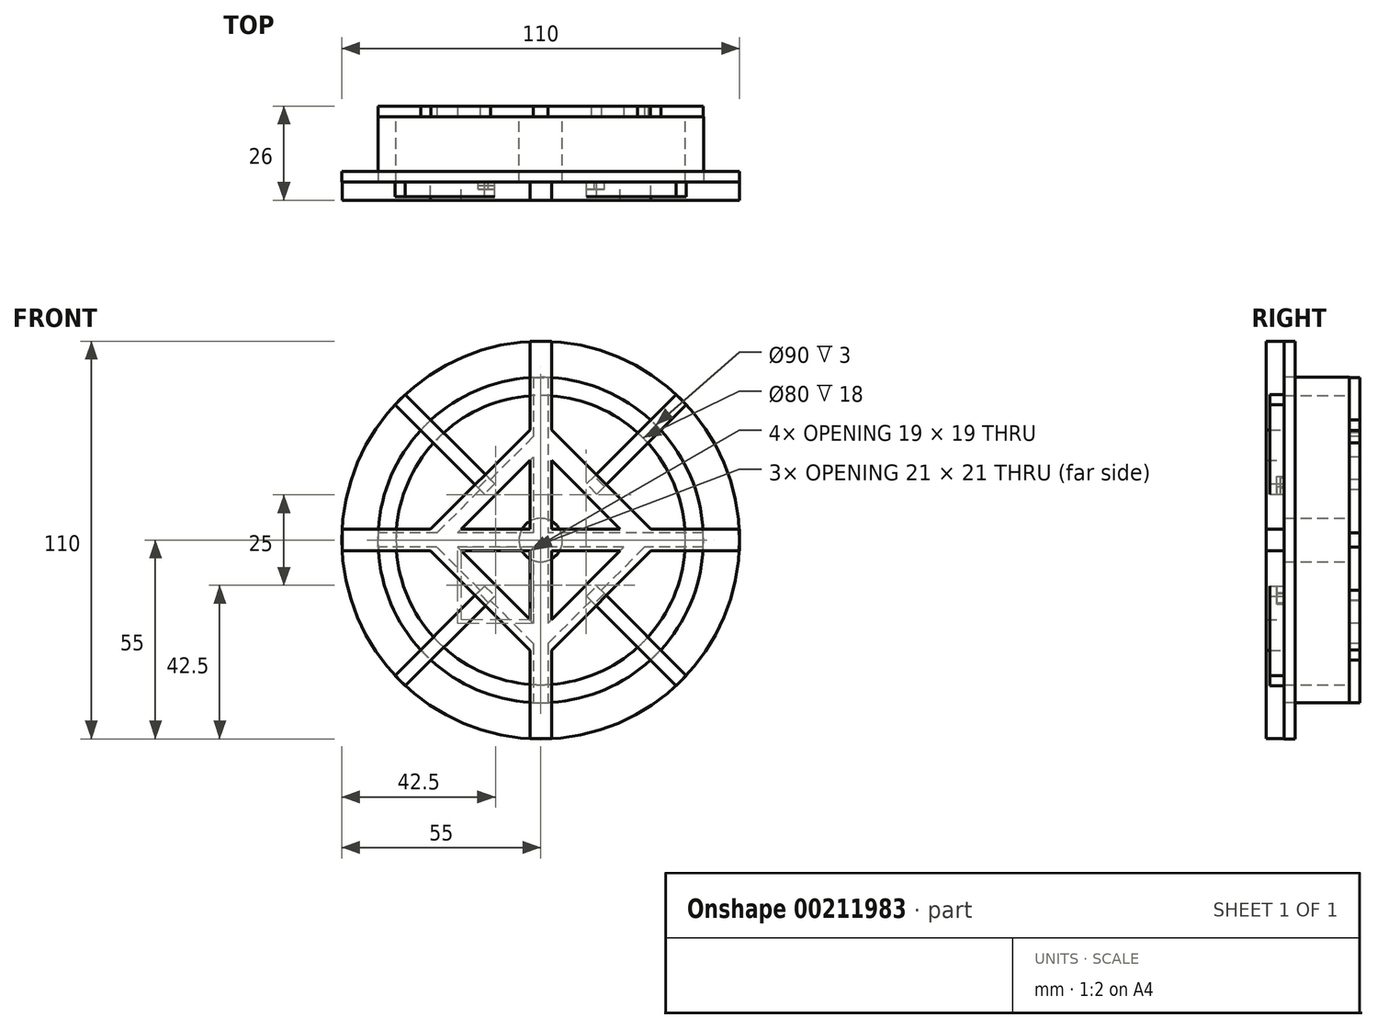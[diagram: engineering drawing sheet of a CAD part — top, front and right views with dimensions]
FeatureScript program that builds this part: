
annotation { "Feature Type Name" : "Feature", "Feature Type Description" : "" }
export const myFeature = defineFeature(function(context is Context, id is Id, definition is map)
    precondition{}
    {
        {
            var Q0;
            Q0=qCreatedBy(makeId("Front.planeOp"),FACE);
            var sketch = newSketch(context, id + "F0", { "sketchPlane" : qUnion([Q0])});
            skCircle(sketch, "E0", {"center": v(0, 0) * mm, "radius": 55 * mm});
            skCircle(sketch, "E1", {"center": v(0, 0) * mm, "radius": 45 * mm});
            skCircle(sketch, "E2", {"center": v(0, 0) * mm, "radius": 6 * mm});
            skCircle(sketch, "E3", {"center": v(0, 0) * mm, "radius": 40 * mm});
            skSolve(sketch);
        }
        {
            var Q0;
            Q0=makeQuery(id+"F0.imprint","IMPRINT",FACE,{"disambiguationData":[TD([[makeQuery(id+"F0.imprint","IMPRINT",EDGE,{"derivedFrom":sQuery(id+"F0.wireOp",EDGE,"E2")}),1.0]])]});
            var Q1;
            Q1=makeQuery(id+"F0.imprint","IMPRINT",FACE,{"disambiguationData":[TD([[makeQuery(id+"F0.imprint","IMPRINT",EDGE,{"derivedFrom":sQuery(id+"F0.wireOp",EDGE,"E1")}),1.0]])]});
            extrude(context, id + "F1", {"entities" : qUnion([Q0, Q1]), "depth" : 18 * mm});
        }
        {
            var Q0;
            Q0=makeQuery(id+"F1.opExtrude","CAP_FACE",FACE,{"disambiguationData":[OSD([sQuery(id+"F0.wireOp",EDGE,"E1"),sQuery(id+"F0.wireOp",EDGE,"E3")])],"isStart":false});
            var sketch = newSketch(context, id + "F2", { "sketchPlane" : qUnion([Q0])});
            skCircle(sketch, "E4", {"center": v(0, 0) * mm, "radius": 55 * mm});
            skCircle(sketch, "E5", {"center": v(0, 0) * mm, "radius": 45 * mm});
            skSolve(sketch);
        }
        {
            var Q0;
            Q0=makeQuery(id+"F2.imprint","IMPRINT",FACE,{"disambiguationData":[TD([[makeQuery(id+"F2.imprint","IMPRINT",EDGE,{"derivedFrom":sQuery(id+"F2.wireOp",EDGE,"E4")}),1.0]])]});
            extrude(context, id + "F3", {"entities" : qUnion([Q0]), "oppositeDirection" : true, "depth" : 3 * mm});
        }
        {
            var Q0;
            Q0=makeQuery(id+"F3.opExtrude","CAP_FACE",FACE,{"disambiguationData":[OSD([sQuery(id+"F2.wireOp",EDGE,"E4"),sQuery(id+"F2.wireOp",EDGE,"E5")])],"isStart":true});
            var sketch = newSketch(context, id + "F4", { "sketchPlane" : qUnion([Q0])});
            skLineSegment(sketch, "E6.bottom", {"start": v(-54.92, -3) * mm, "end": v(54.92, -3) * mm});
            skLineSegment(sketch, "E6.top", {"start": v(-54.92, 3) * mm, "end": v(54.92, 3) * mm});
            skLineSegment(sketch, "E6.left", {"start": v(-54.92, -3) * mm, "end": v(-54.92, 3) * mm});
            skLineSegment(sketch, "E6.right", {"start": v(54.92, -3) * mm, "end": v(54.92, 3) * mm});
            skPoint(sketch, "E6.middle", {"position": v(0, 0) * mm});
            skLineSegment(sketch, "E7.bottom", {"start": v(3, 54.92) * mm, "end": v(-3, 54.92) * mm});
            skLineSegment(sketch, "E7.top", {"start": v(3, -54.92) * mm, "end": v(-3, -54.92) * mm});
            skLineSegment(sketch, "E7.left", {"start": v(3, 54.92) * mm, "end": v(3, -54.92) * mm});
            skLineSegment(sketch, "E7.right", {"start": v(-3, 54.92) * mm, "end": v(-3, -54.92) * mm});
            skLineSegment(sketch, "E8", {"start": v(-142.2, 0) * mm, "end": v(132.52, 0) * mm, "construction": true});
            skLineSegment(sketch, "E9", {"start": v(0, 134.39) * mm, "end": v(0, -130.48) * mm, "construction": true});
            skLineSegment(sketch, "E10", {"start": v(0, 25) * mm, "end": v(-25, 0) * mm});
            skLineSegment(sketch, "E11", {"start": v(-25, 0) * mm, "end": v(0, -25) * mm});
            skLineSegment(sketch, "E12", {"start": v(0, -25) * mm, "end": v(25, 0) * mm});
            skLineSegment(sketch, "E13", {"start": v(25, 0) * mm, "end": v(0, 25) * mm});
            skLineSegment(sketch, "E14", {"start": v(0, 33.49) * mm, "end": v(-33.49, 0) * mm});
            skLineSegment(sketch, "E15", {"start": v(-33.49, 0) * mm, "end": v(0, -33.49) * mm});
            skLineSegment(sketch, "E16", {"start": v(0, -33.49) * mm, "end": v(33.49, 0) * mm});
            skLineSegment(sketch, "E17", {"start": v(33.49, 0) * mm, "end": v(0, 33.49) * mm});
            skSolve(sketch);
        }
        {
            var Q0;
            {var subQ0=sQuery(id+"F4.wireOp",EDGE,"E7.right");var subQ1=sQuery(id+"F4.wireOp",EDGE,"E6.bottom");var subQ2=makeQuery(id+"F4.imprint","INTERSECT",VERTEX,{"derivedFrom":[subQ1,subQ0]});Q0=makeQuery(id+"F4.imprint","IMPRINT",FACE,{"disambiguationData":[TD([[makeQuery(id+"F4.imprint","IMPRINT",EDGE,{"disambiguationData":[TD([[subQ2,-1.0]])],"derivedFrom":subQ1}),1.0]])]});}
            var Q1;
            {var subQ0=sQuery(id+"F4.wireOp",EDGE,"E6.left");Q1=makeQuery(id+"F4.imprint","IMPRINT",FACE,{"disambiguationData":[TD([[makeQuery(id+"F4.imprint","IMPRINT",EDGE,{"derivedFrom":subQ0}),-1.0]])]});}
            var Q2;
            {var subQ0=sQuery(id+"F4.wireOp",EDGE,"E7.right");var subQ1=sQuery(id+"F4.wireOp",EDGE,"E6.bottom");var subQ2=makeQuery(id+"F4.imprint","INTERSECT",VERTEX,{"derivedFrom":[subQ1,subQ0]});Q2=makeQuery(id+"F4.imprint","IMPRINT",FACE,{"disambiguationData":[TD([[makeQuery(id+"F4.imprint","IMPRINT",EDGE,{"disambiguationData":[TD([[subQ2,1.0]])],"derivedFrom":subQ1}),1.0]])]});}
            var Q3;
            {var subQ0=sQuery(id+"F4.wireOp",EDGE,"E7.right");var subQ1=sQuery(id+"F4.wireOp",EDGE,"E6.bottom");var subQ2=makeQuery(id+"F4.imprint","INTERSECT",VERTEX,{"derivedFrom":[subQ1,subQ0]});Q3=makeQuery(id+"F4.imprint","IMPRINT",FACE,{"disambiguationData":[TD([[makeQuery(id+"F4.imprint","IMPRINT",EDGE,{"disambiguationData":[TD([[subQ2,-1.0]])],"derivedFrom":subQ1}),-1.0]])]});}
            var Q4;
            {var subQ0=sQuery(id+"F4.wireOp",EDGE,"E7.left");var subQ1=sQuery(id+"F4.wireOp",EDGE,"E6.bottom");var subQ2=makeQuery(id+"F4.imprint","INTERSECT",VERTEX,{"derivedFrom":[subQ1,subQ0]});Q4=makeQuery(id+"F4.imprint","IMPRINT",FACE,{"disambiguationData":[TD([[makeQuery(id+"F4.imprint","IMPRINT",EDGE,{"disambiguationData":[TD([[subQ2,-1.0]])],"derivedFrom":subQ1}),1.0]])]});}
            var Q5;
            {var subQ0=sQuery(id+"F4.wireOp",EDGE,"E6.right");Q5=makeQuery(id+"F4.imprint","IMPRINT",FACE,{"disambiguationData":[TD([[makeQuery(id+"F4.imprint","IMPRINT",EDGE,{"derivedFrom":subQ0}),1.0]])]});}
            var Q6;
            {var subQ0=sQuery(id+"F4.wireOp",EDGE,"E7.bottom");Q6=makeQuery(id+"F4.imprint","IMPRINT",FACE,{"disambiguationData":[TD([[makeQuery(id+"F4.imprint","IMPRINT",EDGE,{"derivedFrom":subQ0}),1.0]])]});}
            var Q7;
            {var subQ0=sQuery(id+"F4.wireOp",EDGE,"E7.top");Q7=makeQuery(id+"F4.imprint","IMPRINT",FACE,{"disambiguationData":[TD([[makeQuery(id+"F4.imprint","IMPRINT",EDGE,{"derivedFrom":subQ0}),-1.0]])]});}
            var Q8;
            {var subQ0=sQuery(id+"F4.wireOp",EDGE,"E7.right");var subQ1=sQuery(id+"F4.wireOp",EDGE,"E6.top");var subQ2=makeQuery(id+"F4.imprint","INTERSECT",VERTEX,{"derivedFrom":[subQ1,subQ0]});Q8=makeQuery(id+"F4.imprint","IMPRINT",FACE,{"disambiguationData":[TD([[makeQuery(id+"F4.imprint","IMPRINT",EDGE,{"disambiguationData":[TD([[subQ2,-1.0]])],"derivedFrom":subQ1}),1.0]])]});}
            var Q9;
            {var subQ0=sQuery(id+"F4.wireOp",EDGE,"E15");var subQ5=sQuery(id+"F4.wireOp",EDGE,"E6.bottom");var subQ6=makeQuery(id+"F4.imprint","INTERSECT",VERTEX,{"derivedFrom":[subQ5,subQ0]});Q9=makeQuery(id+"F4.imprint","IMPRINT",FACE,{"disambiguationData":[TD([[makeQuery(id+"F4.imprint","IMPRINT",EDGE,{"disambiguationData":[TD([[subQ6,1.0]])],"derivedFrom":subQ5}),1.0]])]});}
            var Q10;
            {var subQ3=sQuery(id+"F4.wireOp",EDGE,"E6.bottom");var subQ9=sQuery(id+"F4.wireOp",EDGE,"E15");var subQ10=makeQuery(id+"F4.imprint","INTERSECT",VERTEX,{"derivedFrom":[subQ3,subQ9]});Q10=makeQuery(id+"F4.imprint","IMPRINT",FACE,{"disambiguationData":[TD([[makeQuery(id+"F4.imprint","IMPRINT",EDGE,{"disambiguationData":[TD([[subQ10,-1.0]])],"derivedFrom":subQ3}),1.0]])]});}
            var Q11;
            {var subQ0=sQuery(id+"F4.wireOp",EDGE,"E14");var subQ1=sQuery(id+"F4.wireOp",EDGE,"E6.top");var subQ2=makeQuery(id+"F4.imprint","INTERSECT",VERTEX,{"derivedFrom":[subQ1,subQ0]});Q11=makeQuery(id+"F4.imprint","IMPRINT",FACE,{"disambiguationData":[TD([[makeQuery(id+"F4.imprint","IMPRINT",EDGE,{"disambiguationData":[TD([[subQ2,-1.0]])],"derivedFrom":subQ1}),1.0]])]});}
            var Q12;
            {var subQ0=sQuery(id+"F4.wireOp",EDGE,"E15");var subQ1=sQuery(id+"F4.wireOp",EDGE,"E6.bottom");var subQ2=makeQuery(id+"F4.imprint","INTERSECT",VERTEX,{"derivedFrom":[subQ1,subQ0]});Q12=makeQuery(id+"F4.imprint","IMPRINT",FACE,{"disambiguationData":[TD([[makeQuery(id+"F4.imprint","IMPRINT",EDGE,{"disambiguationData":[TD([[subQ2,-1.0]])],"derivedFrom":subQ1}),-1.0]])]});}
            var Q13;
            {var subQ0=sQuery(id+"F4.wireOp",EDGE,"E12");var subQ1=sQuery(id+"F4.wireOp",EDGE,"E6.bottom");var subQ2=makeQuery(id+"F4.imprint","INTERSECT",VERTEX,{"derivedFrom":[subQ1,subQ0]});Q13=makeQuery(id+"F4.imprint","IMPRINT",FACE,{"disambiguationData":[TD([[makeQuery(id+"F4.imprint","IMPRINT",EDGE,{"disambiguationData":[TD([[subQ2,-1.0]])],"derivedFrom":subQ1}),-1.0]])]});}
            var Q14;
            {var subQ0=sQuery(id+"F4.wireOp",EDGE,"E12");var subQ9=sQuery(id+"F4.wireOp",EDGE,"E7.left");var subQ11=makeQuery(id+"F4.imprint","INTERSECT",VERTEX,{"derivedFrom":[subQ9,subQ0]});Q14=makeQuery(id+"F4.imprint","IMPRINT",FACE,{"disambiguationData":[TD([[makeQuery(id+"F4.imprint","IMPRINT",EDGE,{"disambiguationData":[TD([[subQ11,-1.0]])],"derivedFrom":subQ9}),-1.0]])]});}
            var Q15;
            {var subQ0=sQuery(id+"F4.wireOp",EDGE,"E16");var subQ5=sQuery(id+"F4.wireOp",EDGE,"E7.left");var subQ6=makeQuery(id+"F4.imprint","INTERSECT",VERTEX,{"derivedFrom":[subQ5,subQ0]});Q15=makeQuery(id+"F4.imprint","IMPRINT",FACE,{"disambiguationData":[TD([[makeQuery(id+"F4.imprint","IMPRINT",EDGE,{"disambiguationData":[TD([[subQ6,-1.0]])],"derivedFrom":subQ5}),-1.0]])]});}
            var Q16;
            {var subQ0=sQuery(id+"F4.wireOp",EDGE,"E13");var subQ1=sQuery(id+"F4.wireOp",EDGE,"E6.top");var subQ2=makeQuery(id+"F4.imprint","INTERSECT",VERTEX,{"derivedFrom":[subQ1,subQ0]});Q16=makeQuery(id+"F4.imprint","IMPRINT",FACE,{"disambiguationData":[TD([[makeQuery(id+"F4.imprint","IMPRINT",EDGE,{"disambiguationData":[TD([[subQ2,-1.0]])],"derivedFrom":subQ1}),1.0]])]});}
            var Q17;
            {var subQ1=sQuery(id+"F4.wireOp",EDGE,"E12");var subQ5=sQuery(id+"F4.wireOp",EDGE,"E6.bottom");var subQ6=makeQuery(id+"F4.imprint","INTERSECT",VERTEX,{"derivedFrom":[subQ5,subQ1]});Q17=makeQuery(id+"F4.imprint","IMPRINT",FACE,{"disambiguationData":[TD([[makeQuery(id+"F4.imprint","IMPRINT",EDGE,{"disambiguationData":[TD([[subQ6,-1.0]])],"derivedFrom":subQ5}),1.0]])]});}
            var Q18;
            {var subQ3=sQuery(id+"F4.wireOp",EDGE,"E7.left");var subQ9=sQuery(id+"F4.wireOp",EDGE,"E17");var subQ10=makeQuery(id+"F4.imprint","INTERSECT",VERTEX,{"derivedFrom":[subQ3,subQ9]});Q18=makeQuery(id+"F4.imprint","IMPRINT",FACE,{"disambiguationData":[TD([[makeQuery(id+"F4.imprint","IMPRINT",EDGE,{"disambiguationData":[TD([[subQ10,-1.0]])],"derivedFrom":subQ3}),-1.0]])]});}
            var Q19;
            {var subQ0=sQuery(id+"F4.wireOp",EDGE,"E17");var subQ5=sQuery(id+"F4.wireOp",EDGE,"E7.left");var subQ6=makeQuery(id+"F4.imprint","INTERSECT",VERTEX,{"derivedFrom":[subQ5,subQ0]});Q19=makeQuery(id+"F4.imprint","IMPRINT",FACE,{"disambiguationData":[TD([[makeQuery(id+"F4.imprint","IMPRINT",EDGE,{"disambiguationData":[TD([[subQ6,1.0]])],"derivedFrom":subQ5}),-1.0]])]});}
            var Q20;
            {var subQ1=sQuery(id+"F4.wireOp",EDGE,"E16");var subQ5=sQuery(id+"F4.wireOp",EDGE,"E6.bottom");var subQ6=makeQuery(id+"F4.imprint","INTERSECT",VERTEX,{"derivedFrom":[subQ5,subQ1]});Q20=makeQuery(id+"F4.imprint","IMPRINT",FACE,{"disambiguationData":[TD([[makeQuery(id+"F4.imprint","IMPRINT",EDGE,{"disambiguationData":[TD([[subQ6,-1.0]])],"derivedFrom":subQ5}),1.0]])]});}
            extrude(context, id + "F5", {"entities" : qUnion([Q0, Q1, Q2, Q3, Q4, Q5, Q6, Q7, Q8, Q9, Q10, Q11, Q12, Q13, Q14, Q15, Q16, Q17, Q18, Q19, Q20]), "depth" : 5 * mm});
        }
        {
            var Q0;
            Q0=makeQuery(id+"F3.opExtrude","CAP_FACE",FACE,{"disambiguationData":[OSD([sQuery(id+"F2.wireOp",EDGE,"E4"),sQuery(id+"F2.wireOp",EDGE,"E5")])],"isStart":true});
            var sketch = newSketch(context, id + "F6", { "sketchPlane" : qUnion([Q0])});
            skLineSegment(sketch, "E18", {"start": v(116.81, -116.81) * mm, "end": v(-97.26, 97.26) * mm, "construction": true});
            skLineSegment(sketch, "E19", {"start": v(-138.56, 0) * mm, "end": v(133.7, 0) * mm, "construction": true});
            skLineSegment(sketch, "E20", {"start": v(0, 132.87) * mm, "end": v(0, -131.26) * mm, "construction": true});
            skLineSegment(sketch, "E21", {"start": v(-110.25, -110.25) * mm, "end": v(110.73, 110.73) * mm, "construction": true});
            skLineSegment(sketch, "E22", {"start": v(-15.53, 12.7) * mm, "end": v(-40.28, 37.45) * mm});
            skLineSegment(sketch, "E23", {"start": v(-40.28, 37.45) * mm, "end": v(-37.45, 40.28) * mm});
            skLineSegment(sketch, "E24", {"start": v(-37.45, 40.28) * mm, "end": v(-12.7, 15.53) * mm});
            skLineSegment(sketch, "E25", {"start": v(-12.7, 15.53) * mm, "end": v(-15.53, 12.7) * mm});
            skPoint(sketch, "E26.center", {"position": v(0, -14.16) * mm});
            skPoint(sketch, "E27.center", {"position": v(0, -31.9) * mm});
            skLineSegment(sketch, "E28.1.0", {"start": v(-40.28, -37.45) * mm, "end": v(-15.53, -12.7) * mm});
            skLineSegment(sketch, "E28.1.1", {"start": v(-37.45, -40.28) * mm, "end": v(-40.28, -37.45) * mm});
            skLineSegment(sketch, "E28.1.2", {"start": v(-12.7, -15.53) * mm, "end": v(-37.45, -40.28) * mm});
            skLineSegment(sketch, "E28.1.3", {"start": v(-15.53, -12.7) * mm, "end": v(-12.7, -15.53) * mm});
            skLineSegment(sketch, "E28.2.0", {"start": v(37.45, -40.28) * mm, "end": v(12.7, -15.53) * mm});
            skLineSegment(sketch, "E28.2.1", {"start": v(40.28, -37.45) * mm, "end": v(37.45, -40.28) * mm});
            skLineSegment(sketch, "E28.2.2", {"start": v(15.53, -12.7) * mm, "end": v(40.28, -37.45) * mm});
            skLineSegment(sketch, "E28.2.3", {"start": v(12.7, -15.53) * mm, "end": v(15.53, -12.7) * mm});
            skLineSegment(sketch, "E28.3.0", {"start": v(40.28, 37.45) * mm, "end": v(15.53, 12.7) * mm});
            skLineSegment(sketch, "E28.3.1", {"start": v(37.45, 40.28) * mm, "end": v(40.28, 37.45) * mm});
            skLineSegment(sketch, "E28.3.2", {"start": v(12.7, 15.53) * mm, "end": v(37.45, 40.28) * mm});
            skLineSegment(sketch, "E28.3.3", {"start": v(15.53, 12.7) * mm, "end": v(12.7, 15.53) * mm});
            skPoint(sketch, "E28.center", {"position": v(0, 0) * mm});
            skSolve(sketch);
        }
        {
            var Q0;
            Q0 = qSketchRegion(id + "F6", true);
            extrude(context, id + "F7", {"entities" : qUnion([Q0]), "depth" : 4 * mm});
        }
        {
            var Q0;
            Q0=makeQuery(id+"F7.opExtrude","CAP_FACE",FACE,{"disambiguationData":[OSD([sQuery(id+"F6.wireOp",EDGE,"E22"),sQuery(id+"F6.wireOp",EDGE,"E23"),sQuery(id+"F6.wireOp",EDGE,"E24"),sQuery(id+"F6.wireOp",EDGE,"E25")])],"isStart":true});
            var sketch = newSketch(context, id + "F8", { "sketchPlane" : qUnion([Q0])});
            skLineSegment(sketch, "E29", {"start": v(14.47, 17.3) * mm, "end": v(12.7, 15.53) * mm});
            skLineSegment(sketch, "E30", {"start": v(12.7, 15.53) * mm, "end": v(15.53, 12.7) * mm});
            skLineSegment(sketch, "E31", {"start": v(15.53, 12.7) * mm, "end": v(17.3, 14.47) * mm});
            skLineSegment(sketch, "E32", {"start": v(17.3, 14.47) * mm, "end": v(14.47, 17.3) * mm});
            skSolve(sketch);
        }
        {
            var Q0;
            Q0=makeQuery(id+"F8.imprint","IMPRINT",FACE,{"disambiguationData":[TD([[makeQuery(id+"F8.imprint","IMPRINT",EDGE,{"derivedFrom":sQuery(id+"F8.wireOp",EDGE,"E29")}),1.0]])]});
            extrude(context, id + "F9", {"entities" : qUnion([Q0]), "operationType" : NewBodyOperationType.REMOVE, "oppositeDirection" : true, "depth" : 1 * mm});
        }
        {
            var Q0;
            Q0=makeQuery(id+"F7.opExtrude","CAP_FACE",FACE,{"disambiguationData":[OSD([sQuery(id+"F6.wireOp",EDGE,"E28.1.0"),sQuery(id+"F6.wireOp",EDGE,"E28.1.1"),sQuery(id+"F6.wireOp",EDGE,"E28.1.2"),sQuery(id+"F6.wireOp",EDGE,"E28.1.3")])],"isStart":true});
            var sketch = newSketch(context, id + "F10", { "sketchPlane" : qUnion([Q0])});
            skLineSegment(sketch, "E33", {"start": v(15.53, -12.7) * mm, "end": v(12.7, -15.53) * mm});
            skLineSegment(sketch, "E34", {"start": v(12.7, -15.53) * mm, "end": v(14.47, -17.3) * mm});
            skLineSegment(sketch, "E35", {"start": v(14.47, -17.3) * mm, "end": v(17.3, -14.47) * mm});
            skLineSegment(sketch, "E36", {"start": v(17.3, -14.47) * mm, "end": v(15.53, -12.7) * mm});
            skSolve(sketch);
        }
        {
            var Q0;
            Q0 = qSketchRegion(id + "F10", true);
            extrude(context, id + "F11", {"entities" : qUnion([Q0]), "operationType" : NewBodyOperationType.REMOVE, "oppositeDirection" : true, "depth" : 2 * mm});
        }
        {
            var Q0;
            Q0=makeQuery(id+"F7.opExtrude","CAP_FACE",FACE,{"disambiguationData":[OSD([sQuery(id+"F6.wireOp",EDGE,"E28.2.0"),sQuery(id+"F6.wireOp",EDGE,"E28.2.1"),sQuery(id+"F6.wireOp",EDGE,"E28.2.2"),sQuery(id+"F6.wireOp",EDGE,"E28.2.3")])],"isStart":true});
            var sketch = newSketch(context, id + "F12", { "sketchPlane" : qUnion([Q0])});
            skLineSegment(sketch, "E37", {"start": v(-12.7, -15.53) * mm, "end": v(-15.53, -12.7) * mm});
            skLineSegment(sketch, "E38", {"start": v(-15.53, -12.7) * mm, "end": v(-17.65, -14.82) * mm});
            skLineSegment(sketch, "E39", {"start": v(-17.65, -14.82) * mm, "end": v(-14.82, -17.65) * mm});
            skLineSegment(sketch, "E40", {"start": v(-14.82, -17.65) * mm, "end": v(-12.7, -15.53) * mm});
            skSolve(sketch);
        }
        {
            var Q0;
            Q0=makeQuery(id+"F12.imprint","IMPRINT",FACE,{"disambiguationData":[TD([[makeQuery(id+"F12.imprint","IMPRINT",EDGE,{"derivedFrom":sQuery(id+"F12.wireOp",EDGE,"E37")}),1.0]])]});
            extrude(context, id + "F13", {"entities" : qUnion([Q0]), "operationType" : NewBodyOperationType.REMOVE, "oppositeDirection" : true, "depth" : 2 * mm});
        }
        {
            var Q0;
            Q0=makeQuery(id+"F7.opExtrude","CAP_FACE",FACE,{"disambiguationData":[OSD([sQuery(id+"F6.wireOp",EDGE,"E28.3.0"),sQuery(id+"F6.wireOp",EDGE,"E28.3.1"),sQuery(id+"F6.wireOp",EDGE,"E28.3.2"),sQuery(id+"F6.wireOp",EDGE,"E28.3.3")])],"isStart":true});
            var sketch = newSketch(context, id + "F14", { "sketchPlane" : qUnion([Q0])});
            skLineSegment(sketch, "E41", {"start": v(-12.7, 15.53) * mm, "end": v(-15.53, 12.7) * mm});
            skLineSegment(sketch, "E42", {"start": v(-15.53, 12.7) * mm, "end": v(-17.65, 14.82) * mm});
            skLineSegment(sketch, "E43", {"start": v(-17.65, 14.82) * mm, "end": v(-14.82, 17.65) * mm});
            skLineSegment(sketch, "E44", {"start": v(-14.82, 17.65) * mm, "end": v(-12.7, 15.53) * mm});
            skSolve(sketch);
        }
        {
            var Q0;
            Q0 = qSketchRegion(id + "F14", true);
            extrude(context, id + "F15", {"entities" : qUnion([Q0]), "operationType" : NewBodyOperationType.REMOVE, "oppositeDirection" : true, "depth" : 2 * mm});
        }
        {
            var Q0;
            Q0=makeQuery(id+"F1.opExtrude","CAP_FACE",FACE,{"disambiguationData":[OSD([sQuery(id+"F0.wireOp",EDGE,"E1"),sQuery(id+"F0.wireOp",EDGE,"E3")])],"isStart":true});
            var sketch = newSketch(context, id + "F16", { "sketchPlane" : qUnion([Q0])});
            skLineSegment(sketch, "E45", {"start": v(-62.44, 0) * mm, "end": v(62.34, 0) * mm, "construction": true});
            skLineSegment(sketch, "E46", {"start": v(0, -61) * mm, "end": v(0, 59.36) * mm, "construction": true});
            skLineSegment(sketch, "E47", {"start": v(-48.21, 48.21) * mm, "end": v(50.02, -50.02) * mm, "construction": true});
            skLineSegment(sketch, "E48", {"start": v(46.02, 46.02) * mm, "end": v(-48.3, -48.3) * mm, "construction": true});
            skLineSegment(sketch, "E49.bottom", {"start": v(-44.96, -2) * mm, "end": v(44.96, -2) * mm});
            skLineSegment(sketch, "E49.top", {"start": v(-44.96, 2) * mm, "end": v(44.96, 2) * mm});
            skLineSegment(sketch, "E49.left", {"start": v(-44.96, -2) * mm, "end": v(-44.96, 2) * mm});
            skLineSegment(sketch, "E49.right", {"start": v(44.96, -2) * mm, "end": v(44.96, 2) * mm});
            skPoint(sketch, "E49.middle", {"position": v(0, 0) * mm});
            skLineSegment(sketch, "E50.bottom", {"start": v(2, 44.96) * mm, "end": v(-2, 44.96) * mm});
            skLineSegment(sketch, "E50.top", {"start": v(2, -44.96) * mm, "end": v(-2, -44.96) * mm});
            skLineSegment(sketch, "E50.left", {"start": v(2, 44.96) * mm, "end": v(2, -44.96) * mm});
            skLineSegment(sketch, "E50.right", {"start": v(-2, 44.96) * mm, "end": v(-2, -44.96) * mm});
            skLineSegment(sketch, "E51", {"start": v(0, 30.66) * mm, "end": v(-30.66, 0) * mm});
            skLineSegment(sketch, "E52", {"start": v(-30.66, 0) * mm, "end": v(0, -30.66) * mm});
            skLineSegment(sketch, "E53", {"start": v(0, -30.66) * mm, "end": v(30.66, 0) * mm});
            skLineSegment(sketch, "E54", {"start": v(30.66, 0) * mm, "end": v(0, 30.66) * mm});
            skLineSegment(sketch, "E55", {"start": v(0, 25) * mm, "end": v(-25, 0) * mm});
            skLineSegment(sketch, "E56", {"start": v(-25, 0) * mm, "end": v(0, -25) * mm});
            skLineSegment(sketch, "E57", {"start": v(0, -25) * mm, "end": v(25, 0) * mm});
            skLineSegment(sketch, "E58", {"start": v(25, 0) * mm, "end": v(0, 25) * mm});
            skLineSegment(sketch, "E59", {"start": v(-16.74, 13.91) * mm, "end": v(-33.2, 30.37) * mm});
            skLineSegment(sketch, "E60", {"start": v(-33.2, 30.37) * mm, "end": v(-30.37, 33.2) * mm});
            skLineSegment(sketch, "E61", {"start": v(-30.37, 33.2) * mm, "end": v(-13.91, 16.74) * mm});
            skLineSegment(sketch, "E62", {"start": v(-13.91, 16.74) * mm, "end": v(-16.74, 13.91) * mm});
            skLineSegment(sketch, "E63.1.0", {"start": v(-33.19, -30.36) * mm, "end": v(-16.73, -13.9) * mm});
            skLineSegment(sketch, "E63.1.1", {"start": v(-13.9, -16.73) * mm, "end": v(-30.36, -33.19) * mm});
            skLineSegment(sketch, "E63.1.2", {"start": v(-30.36, -33.19) * mm, "end": v(-33.19, -30.36) * mm});
            skLineSegment(sketch, "E63.2.0", {"start": v(30.37, -33.17) * mm, "end": v(13.91, -16.71) * mm});
            skLineSegment(sketch, "E63.2.1", {"start": v(16.74, -13.88) * mm, "end": v(33.2, -30.34) * mm});
            skLineSegment(sketch, "E63.2.2", {"start": v(33.2, -30.34) * mm, "end": v(30.37, -33.17) * mm});
            skLineSegment(sketch, "E63.3.0", {"start": v(33.19, 30.4) * mm, "end": v(16.73, 13.93) * mm});
            skLineSegment(sketch, "E63.3.1", {"start": v(13.9, 16.76) * mm, "end": v(30.36, 33.22) * mm});
            skLineSegment(sketch, "E63.3.2", {"start": v(30.36, 33.22) * mm, "end": v(33.19, 30.4) * mm});
            skPoint(sketch, "E63.center", {"position": v(0, 0.02) * mm});
            skSolve(sketch);
        }
        {
            var Q0;
            {var subQ0=sQuery(id+"F16.wireOp",EDGE,"E62");Q0=makeQuery(id+"F16.imprint","IMPRINT",FACE,{"disambiguationData":[TD([[makeQuery(id+"F16.imprint","IMPRINT",EDGE,{"derivedFrom":subQ0}),-1.0]])]});}
            var Q1;
            {var subQ0=sQuery(id+"F16.wireOp",EDGE,"E60");Q1=makeQuery(id+"F16.imprint","IMPRINT",FACE,{"disambiguationData":[TD([[makeQuery(id+"F16.imprint","IMPRINT",EDGE,{"derivedFrom":subQ0}),-1.0]])]});}
            var Q2;
            {var subQ0=sQuery(id+"F16.wireOp",EDGE,"E50.bottom");Q2=makeQuery(id+"F16.imprint","IMPRINT",FACE,{"disambiguationData":[TD([[makeQuery(id+"F16.imprint","IMPRINT",EDGE,{"derivedFrom":subQ0}),1.0]])]});}
            var Q3;
            {var subQ0=sQuery(id+"F16.wireOp",EDGE,"E54");var subQ3=sQuery(id+"F16.wireOp",EDGE,"E50.left");var subQ4=makeQuery(id+"F16.imprint","INTERSECT",VERTEX,{"derivedFrom":[subQ3,subQ0]});Q3=makeQuery(id+"F16.imprint","IMPRINT",FACE,{"disambiguationData":[TD([[makeQuery(id+"F16.imprint","IMPRINT",EDGE,{"disambiguationData":[TD([[subQ4,1.0]])],"derivedFrom":subQ3}),-1.0]])]});}
            var Q4;
            {var subQ0=sQuery(id+"F16.wireOp",EDGE,"E63.3.2");Q4=makeQuery(id+"F16.imprint","IMPRINT",FACE,{"disambiguationData":[TD([[makeQuery(id+"F16.imprint","IMPRINT",EDGE,{"derivedFrom":subQ0}),-1.0]])]});}
            var Q5;
            {var subQ0=sQuery(id+"F16.wireOp",EDGE,"E63.3.0");var subQ1=sQuery(id+"F16.wireOp",EDGE,"E54");var subQ2=makeQuery(id+"F16.imprint","INTERSECT",VERTEX,{"derivedFrom":[subQ1,subQ0]});Q5=makeQuery(id+"F16.imprint","IMPRINT",FACE,{"disambiguationData":[TD([[makeQuery(id+"F16.imprint","IMPRINT",EDGE,{"disambiguationData":[TD([[subQ2,-1.0]])],"derivedFrom":subQ1}),-1.0]])]});}
            var Q6;
            {var subQ2=sQuery(id+"F16.wireOp",EDGE,"E49.top");var subQ6=sQuery(id+"F16.wireOp",EDGE,"E58");var subQ9=makeQuery(id+"F16.imprint","INTERSECT",VERTEX,{"derivedFrom":[subQ2,subQ6]});Q6=makeQuery(id+"F16.imprint","IMPRINT",FACE,{"disambiguationData":[TD([[makeQuery(id+"F16.imprint","IMPRINT",EDGE,{"disambiguationData":[TD([[subQ9,-1.0]])],"derivedFrom":subQ2}),1.0]])]});}
            var Q7;
            {var subQ0=sQuery(id+"F16.wireOp",EDGE,"E54");var subQ3=sQuery(id+"F16.wireOp",EDGE,"E50.left");var subQ4=makeQuery(id+"F16.imprint","INTERSECT",VERTEX,{"derivedFrom":[subQ3,subQ0]});Q7=makeQuery(id+"F16.imprint","IMPRINT",FACE,{"disambiguationData":[TD([[makeQuery(id+"F16.imprint","IMPRINT",EDGE,{"disambiguationData":[TD([[subQ4,-1.0]])],"derivedFrom":subQ3}),-1.0]])]});}
            var Q8;
            {var subQ0=sQuery(id+"F16.wireOp",EDGE,"E62");Q8=makeQuery(id+"F16.imprint","IMPRINT",FACE,{"disambiguationData":[TD([[makeQuery(id+"F16.imprint","IMPRINT",EDGE,{"derivedFrom":subQ0}),1.0]])]});}
            var Q9;
            {var subQ0=sQuery(id+"F16.wireOp",EDGE,"E52");var subQ3=sQuery(id+"F16.wireOp",EDGE,"E49.bottom");var subQ4=makeQuery(id+"F16.imprint","INTERSECT",VERTEX,{"derivedFrom":[subQ3,subQ0]});Q9=makeQuery(id+"F16.imprint","IMPRINT",FACE,{"disambiguationData":[TD([[makeQuery(id+"F16.imprint","IMPRINT",EDGE,{"disambiguationData":[TD([[subQ4,-1.0]])],"derivedFrom":subQ3}),1.0]])]});}
            var Q10;
            {var subQ0=sQuery(id+"F16.wireOp",EDGE,"E52");var subQ3=sQuery(id+"F16.wireOp",EDGE,"E49.bottom");var subQ4=makeQuery(id+"F16.imprint","INTERSECT",VERTEX,{"derivedFrom":[subQ3,subQ0]});Q10=makeQuery(id+"F16.imprint","IMPRINT",FACE,{"disambiguationData":[TD([[makeQuery(id+"F16.imprint","IMPRINT",EDGE,{"disambiguationData":[TD([[subQ4,1.0]])],"derivedFrom":subQ3}),1.0]])]});}
            var Q11;
            {var subQ0=sQuery(id+"F16.wireOp",EDGE,"E52");var subQ3=sQuery(id+"F16.wireOp",EDGE,"E49.bottom");var subQ4=makeQuery(id+"F16.imprint","INTERSECT",VERTEX,{"derivedFrom":[subQ3,subQ0]});Q11=makeQuery(id+"F16.imprint","IMPRINT",FACE,{"disambiguationData":[TD([[makeQuery(id+"F16.imprint","IMPRINT",EDGE,{"disambiguationData":[TD([[subQ4,-1.0]])],"derivedFrom":subQ3}),-1.0]])]});}
            var Q12;
            {var subQ5=sQuery(id+"F16.wireOp",EDGE,"E56");var subQ7=sQuery(id+"F16.wireOp",EDGE,"E49.bottom");var subQ9=makeQuery(id+"F16.imprint","INTERSECT",VERTEX,{"derivedFrom":[subQ7,subQ5]});Q12=makeQuery(id+"F16.imprint","IMPRINT",FACE,{"disambiguationData":[TD([[makeQuery(id+"F16.imprint","IMPRINT",EDGE,{"disambiguationData":[TD([[subQ9,-1.0]])],"derivedFrom":subQ7}),1.0]])]});}
            var Q13;
            {var subQ3=sQuery(id+"F16.wireOp",EDGE,"E49.bottom");var subQ5=sQuery(id+"F16.wireOp",EDGE,"E50.left");var subQ6=makeQuery(id+"F16.imprint","INTERSECT",VERTEX,{"derivedFrom":[subQ3,subQ5]});Q13=makeQuery(id+"F16.imprint","IMPRINT",FACE,{"disambiguationData":[TD([[makeQuery(id+"F16.imprint","IMPRINT",EDGE,{"disambiguationData":[TD([[subQ6,-1.0]])],"derivedFrom":subQ3}),1.0]])]});}
            var Q14;
            {var subQ3=sQuery(id+"F16.wireOp",EDGE,"E50.right");var subQ5=sQuery(id+"F16.wireOp",EDGE,"E49.top");var subQ6=makeQuery(id+"F16.imprint","INTERSECT",VERTEX,{"derivedFrom":[subQ5,subQ3]});Q14=makeQuery(id+"F16.imprint","IMPRINT",FACE,{"disambiguationData":[TD([[makeQuery(id+"F16.imprint","IMPRINT",EDGE,{"disambiguationData":[TD([[subQ6,-1.0]])],"derivedFrom":subQ5}),1.0]])]});}
            var Q15;
            {var subQ1=sQuery(id+"F16.wireOp",EDGE,"E53");var subQ5=sQuery(id+"F16.wireOp",EDGE,"E49.bottom");var subQ6=makeQuery(id+"F16.imprint","INTERSECT",VERTEX,{"derivedFrom":[subQ5,subQ1]});Q15=makeQuery(id+"F16.imprint","IMPRINT",FACE,{"disambiguationData":[TD([[makeQuery(id+"F16.imprint","IMPRINT",EDGE,{"disambiguationData":[TD([[subQ6,-1.0]])],"derivedFrom":subQ5}),1.0]])]});}
            var Q16;
            {var subQ5=sQuery(id+"F16.wireOp",EDGE,"E49.bottom");var subQ9=sQuery(id+"F16.wireOp",EDGE,"E57");var subQ10=makeQuery(id+"F16.imprint","INTERSECT",VERTEX,{"derivedFrom":[subQ5,subQ9]});Q16=makeQuery(id+"F16.imprint","IMPRINT",FACE,{"disambiguationData":[TD([[makeQuery(id+"F16.imprint","IMPRINT",EDGE,{"disambiguationData":[TD([[subQ10,-1.0]])],"derivedFrom":subQ5}),1.0]])]});}
            var Q17;
            {var subQ5=sQuery(id+"F16.wireOp",EDGE,"E57");var subQ7=sQuery(id+"F16.wireOp",EDGE,"E49.bottom");var subQ9=makeQuery(id+"F16.imprint","INTERSECT",VERTEX,{"derivedFrom":[subQ7,subQ5]});Q17=makeQuery(id+"F16.imprint","IMPRINT",FACE,{"disambiguationData":[TD([[makeQuery(id+"F16.imprint","IMPRINT",EDGE,{"disambiguationData":[TD([[subQ9,-1.0]])],"derivedFrom":subQ7}),-1.0]])]});}
            var Q18;
            {var subQ0=sQuery(id+"F16.wireOp",EDGE,"E63.2.0");var subQ1=sQuery(id+"F16.wireOp",EDGE,"E53");var subQ2=makeQuery(id+"F16.imprint","INTERSECT",VERTEX,{"derivedFrom":[subQ1,subQ0]});Q18=makeQuery(id+"F16.imprint","IMPRINT",FACE,{"disambiguationData":[TD([[makeQuery(id+"F16.imprint","IMPRINT",EDGE,{"disambiguationData":[TD([[subQ2,-1.0]])],"derivedFrom":subQ1}),-1.0]])]});}
            var Q19;
            {var subQ3=sQuery(id+"F16.wireOp",EDGE,"E50.left");var subQ5=sQuery(id+"F16.wireOp",EDGE,"E57");var subQ6=makeQuery(id+"F16.imprint","INTERSECT",VERTEX,{"derivedFrom":[subQ3,subQ5]});Q19=makeQuery(id+"F16.imprint","IMPRINT",FACE,{"disambiguationData":[TD([[makeQuery(id+"F16.imprint","IMPRINT",EDGE,{"disambiguationData":[TD([[subQ6,-1.0]])],"derivedFrom":subQ3}),-1.0]])]});}
            var Q20;
            {var subQ3=sQuery(id+"F16.wireOp",EDGE,"E50.right");var subQ6=sQuery(id+"F16.wireOp",EDGE,"E49.bottom");var subQ9=makeQuery(id+"F16.imprint","INTERSECT",VERTEX,{"derivedFrom":[subQ6,subQ3]});Q20=makeQuery(id+"F16.imprint","IMPRINT",FACE,{"disambiguationData":[TD([[makeQuery(id+"F16.imprint","IMPRINT",EDGE,{"disambiguationData":[TD([[subQ9,-1.0]])],"derivedFrom":subQ6}),-1.0]])]});}
            var Q21;
            {var subQ0=sQuery(id+"F16.wireOp",EDGE,"E63.1.0");var subQ1=sQuery(id+"F16.wireOp",EDGE,"E52");var subQ2=makeQuery(id+"F16.imprint","INTERSECT",VERTEX,{"derivedFrom":[subQ1,subQ0]});Q21=makeQuery(id+"F16.imprint","IMPRINT",FACE,{"disambiguationData":[TD([[makeQuery(id+"F16.imprint","IMPRINT",EDGE,{"disambiguationData":[TD([[subQ2,-1.0]])],"derivedFrom":subQ1}),-1.0]])]});}
            var Q22;
            {var subQ0=sQuery(id+"F16.wireOp",EDGE,"E63.1.2");Q22=makeQuery(id+"F16.imprint","IMPRINT",FACE,{"disambiguationData":[TD([[makeQuery(id+"F16.imprint","IMPRINT",EDGE,{"derivedFrom":subQ0}),-1.0]])]});}
            var Q23;
            {var subQ0=sQuery(id+"F16.wireOp",EDGE,"E49.left");Q23=makeQuery(id+"F16.imprint","IMPRINT",FACE,{"disambiguationData":[TD([[makeQuery(id+"F16.imprint","IMPRINT",EDGE,{"derivedFrom":subQ0}),-1.0]])]});}
            var Q24;
            {var subQ5=sQuery(id+"F16.wireOp",EDGE,"E63.3.0");var subQ7=sQuery(id+"F16.wireOp",EDGE,"E63.3.2");var subQ9=makeQuery(id+"F16.imprint","INTERSECT",VERTEX,{"derivedFrom":[subQ5,subQ7]});Q24=makeQuery(id+"F16.imprint","IMPRINT",FACE,{"disambiguationData":[TD([[makeQuery(id+"F16.imprint","IMPRINT",EDGE,{"disambiguationData":[TD([[subQ9,-1.0]])],"derivedFrom":subQ5}),-1.0]])]});}
            var Q25;
            {var subQ0=sQuery(id+"F16.wireOp",EDGE,"E63.2.2");Q25=makeQuery(id+"F16.imprint","IMPRINT",FACE,{"disambiguationData":[TD([[makeQuery(id+"F16.imprint","IMPRINT",EDGE,{"derivedFrom":subQ0}),-1.0]])]});}
            var Q26;
            {var subQ0=sQuery(id+"F16.wireOp",EDGE,"E49.right");Q26=makeQuery(id+"F16.imprint","IMPRINT",FACE,{"disambiguationData":[TD([[makeQuery(id+"F16.imprint","IMPRINT",EDGE,{"derivedFrom":subQ0}),1.0]])]});}
            var Q27;
            {var subQ0=sQuery(id+"F16.wireOp",EDGE,"E53");var subQ3=sQuery(id+"F16.wireOp",EDGE,"E50.left");var subQ4=makeQuery(id+"F16.imprint","INTERSECT",VERTEX,{"derivedFrom":[subQ3,subQ0]});Q27=makeQuery(id+"F16.imprint","IMPRINT",FACE,{"disambiguationData":[TD([[makeQuery(id+"F16.imprint","IMPRINT",EDGE,{"disambiguationData":[TD([[subQ4,-1.0]])],"derivedFrom":subQ3}),-1.0]])]});}
            var Q28;
            {var subQ0=sQuery(id+"F16.wireOp",EDGE,"E50.top");Q28=makeQuery(id+"F16.imprint","IMPRINT",FACE,{"disambiguationData":[TD([[makeQuery(id+"F16.imprint","IMPRINT",EDGE,{"derivedFrom":subQ0}),-1.0]])]});}
            var Q29;
            {var subQ0=sQuery(id+"F16.wireOp",EDGE,"E50.right");var subQ1=sQuery(id+"F16.wireOp",EDGE,"E49.bottom");var subQ2=makeQuery(id+"F16.imprint","INTERSECT",VERTEX,{"derivedFrom":[subQ1,subQ0]});Q29=makeQuery(id+"F16.imprint","IMPRINT",FACE,{"disambiguationData":[TD([[makeQuery(id+"F16.imprint","IMPRINT",EDGE,{"disambiguationData":[TD([[subQ2,-1.0]])],"derivedFrom":subQ1}),1.0]])]});}
            extrude(context, id + "F17", {"entities" : qUnion([Q0, Q1, Q2, Q3, Q4, Q5, Q6, Q7, Q8, Q9, Q10, Q11, Q12, Q13, Q14, Q15, Q16, Q17, Q18, Q19, Q20, Q21, Q22, Q23, Q24, Q25, Q26, Q27, Q28, Q29]), "depth" : 3 * mm});
        }
    });
